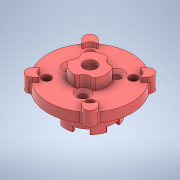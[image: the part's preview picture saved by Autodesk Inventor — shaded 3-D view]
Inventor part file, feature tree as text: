
AUTODESK INVENTOR PART (.ipt)
format: ipt  version: 2020 (Build 240168000, 168)  size: 271,360 bytes
history: native  units: in
note: dims shown in document units (in); Inventor stores cm internally (conversion verified against a paired STEP export)
features: fillet x1
ambient origin geometry x8: Origin, YZ Plane, XZ Plane, XY Plane, X Axis, Y Axis, Z Axis, Center Point
bodies: Solid1 (feature_tree)
feature tree (1):
  fillet  "Fillet3"  [1 undecoded]
note: 1 required parameter value undecoded (feature->parameter linkage not recoverable at this tier; creation-order binding heuristic only, values carry confidence <= 0.55)
